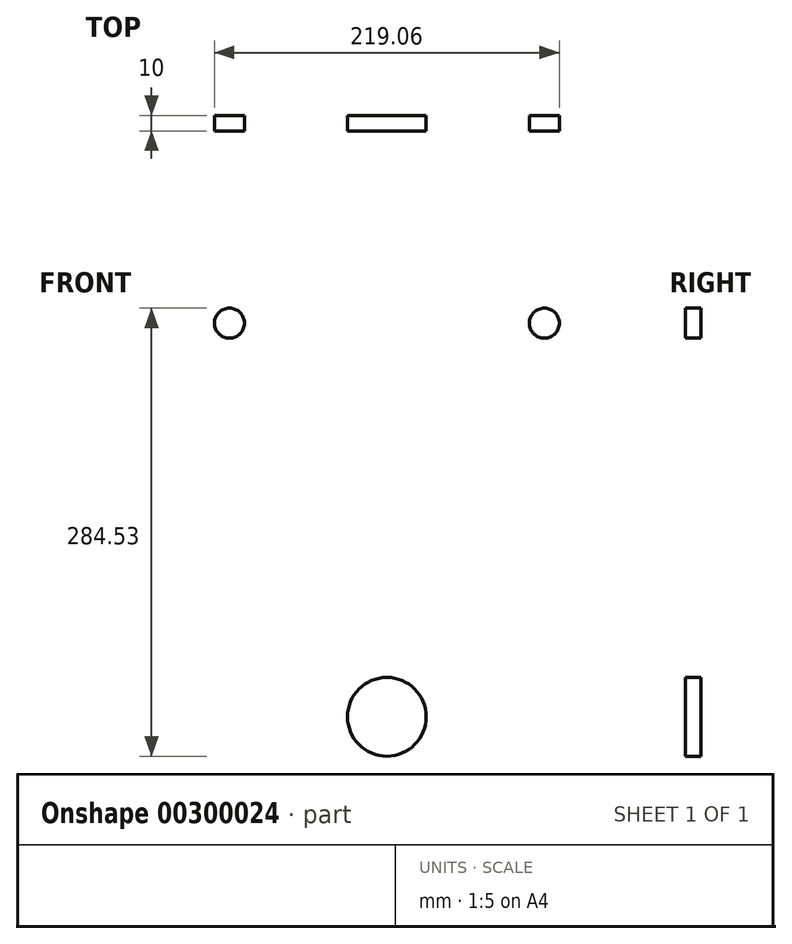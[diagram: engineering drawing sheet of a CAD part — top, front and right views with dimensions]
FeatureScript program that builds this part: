
annotation { "Feature Type Name" : "Feature", "Feature Type Description" : "" }
export const myFeature = defineFeature(function(context is Context, id is Id, definition is map)
    precondition{}
    {
        {
            var Q0;
            Q0=qCreatedBy(makeId("Front.planeOp"),FACE);
            var sketch = newSketch(context, id + "F0", { "sketchPlane" : qUnion([Q0])});
            skCircle(sketch, "E0", {"center": v(0, 0) * mm, "radius": 25 * mm});
            skCircle(sketch, "E1", {"center": v(-100, 250) * mm, "radius": 9.53 * mm});
            skCircle(sketch, "E2.MirrorC", {"center": v(100, 250) * mm, "radius": 9.53 * mm});
            skSolve(sketch);
        }
        {
            var Q0;
            Q0 = qSketchRegion(id + "F0", true);
            extrude(context, id + "F1", {"entities" : qUnion([Q0]), "depth" : 5 * mm, "hasSecondDirection" : true, "secondDirectionOppositeDirection" : true, "secondDirectionDepth" : 5 * mm});
        }
    });
